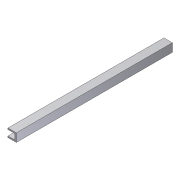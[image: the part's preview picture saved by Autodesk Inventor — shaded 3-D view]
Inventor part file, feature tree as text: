
AUTODESK INVENTOR PART (.ipt)
format: ipt  version: 2012 (Build 160160000, 160)  size: 72,704 bytes
history: native  units: in
note: dims shown in document units (in); Inventor stores cm internally (conversion verified against a paired STEP export)
features: extrude x1, sketch x1
ambient origin geometry x8: Origin, YZ Plane, XZ Plane, XY Plane, X Axis, Y Axis, Z Axis, Center Point
bodies: Solid1 (feature_tree)
feature tree (2):
  extrude  "Extrusion1"  Depth=0.75in
  sketch  "Sketch1"  dims[d0=0.75in d1=0.75in d2=0.125in d3=0.125in d4=0.125in d5=14.0in d6=0.0in]
